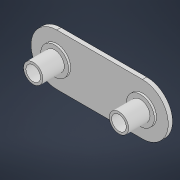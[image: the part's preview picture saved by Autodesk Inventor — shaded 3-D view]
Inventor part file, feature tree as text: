
AUTODESK INVENTOR PART (.ipt)
format: ipt  version: 2022 (Build 260153000, 153)  size: 130,048 bytes
history: native  units: in
note: dims shown in document units (in); Inventor stores cm internally (conversion verified against a paired STEP export)
features: extrude x3, sketch x3, projected_geometry x1
ambient origin geometry x8: Origin, YZ Plane, XZ Plane, XY Plane, X Axis, Y Axis, Z Axis, Center Point
bodies: Solid1 (feature_tree)
feature tree (7):
  extrude  "Extrusion1"  Depth=0.2362in
  extrude  "Extrusion2"  Depth=0.0394in TaperAngle=0.0deg
  extrude  "Extrusion3"  Depth=0.0197in
  sketch  "Sketch1"  dims[d0=0.7874in d1=0.2362in]
  sketch  "Sketch2"  dims[d2=0.1339in d3=0.0394in d4=0.0in]
  sketch  "Sketch3"  dims[d5=0.1772in d6=0.1772in d7=0.2165in d8=0.0in d9=0.2559in d10=0.0197in d11=0.0in]
  projected_geometry  "Projected Loop1"
